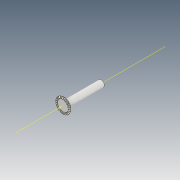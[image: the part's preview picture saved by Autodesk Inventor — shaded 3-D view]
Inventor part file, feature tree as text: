
AUTODESK INVENTOR PART (.ipt)
format: ipt  version: 2021 (Build 250183000, 183)  size: 507,904 bytes
history: native  units: mm
features: other x16, sketch x10, loft x3, pattern_circular x3, extrude x1
ambient origin geometry x6: Origin, XZ Plane, X Axis, Y Axis, Z Axis, Center Point
bodies: Solid1 (feature_tree)
feature tree (33):
  other  "Ponto superior"
  other  "Plano de malha 2"
  other  "Corpo dentado"
  other  "Ponto inicial"
  other  "Plano de dente"
  sketch  "Esboço inicial"  dims[d3=0.6mm]
  other  "Extremidade"
  loft  "Loft"
  pattern_circular  "Circular Pattern"  [2 undecoded]
  sketch  "Esboço 3D direito"  dims[d4=1.194087mm]
  other  "Plano final direito"
  loft  "Transição direita"
  pattern_circular  "Padrão circular direito"  Angle=90.0deg  [1 undecoded]
  sketch  "Esboço 3D esquerdo"  dims[d5=90.0deg]
  other  "Plano final esquerdo"
  loft  "Transição esquerda"
  pattern_circular  "Padrão circular esquerdo"  Angle=360.0deg  [1 undecoded]
  other  "Fixar corpo"
  extrude  "Extrusão1"  Depth=10.0mm
  other  "Plano de malha"
  other  "Plano superior"
  sketch  "Esboço de corpo dentado"  dims[d7=1.663639mm]
  other  "Plano final"
  sketch  "Esboço final"  dims[d8=1.691227mm]
  other  "Helical Curve Left"
  sketch  "Esboço final esquerdo"  dims[d9=4.071779mm]
  sketch  "Esboço de corpo"  dims[d11=0.6198mm]
  sketch  "Sketch6"  dims[d0=4.68mm d1=4.46412mm]
  other  "Srf1"
  other  "Helical Curve Right"
  sketch  "Esboço final direita"  dims[d12=1.281954mm d15=1.303212mm d16=3.137599mm d17=0.0mm d18=90.0deg d19=0.0mm d20=90.0deg d21=260.0mm d22=360.0deg d26=17.944705mm d27=0.309728mm d28=4.68mm d29=-10.47518mm d30=1.281954mm d31=1.303212mm d32=3.137599mm d35=0.0mm d37=0.0mm d39=0.0mm d40=90.0deg d41=260.0mm d42=360.0deg d46=90.0deg d47=90.0deg d48=0.0mm d49=0.0mm d50=90.0deg d51=1.208305mm d52=0.0mm d53=0.0mm d54=0.0mm d56=0.94732mm d57=4.981399mm d58=4.419079mm d59=3.838526mm d60=3.405218mm d61=3.838526mm d62=3.405218mm d65=17.944705mm d66=31.5mm d67=4.68mm d68=-10.47518mm d69=0.309728mm d70=1.303212mm d71=3.137599mm d72=1.281954mm d73=3.405218mm d74=3.838526mm d75=0.0mm d77=0.0mm d79=0.0mm d80=90.0deg d81=260.0mm d82=360.0deg d84=10.0mm d85=20.0mm d86=20.0mm d87=10.0mm d88=0.0mm d89=0.0mm d90=90.0deg d91=90.0deg d92=90.0deg d93=90.0deg d94=12.0mm d95=0.0mm]
  sketch  "Esboço8"  dims[d2=4.8599mm]
  other  "Diâmetro do flanco"
note: 4 required parameter values undecoded (feature->parameter linkage not recoverable at this tier; creation-order binding heuristic only, values carry confidence <= 0.55)
